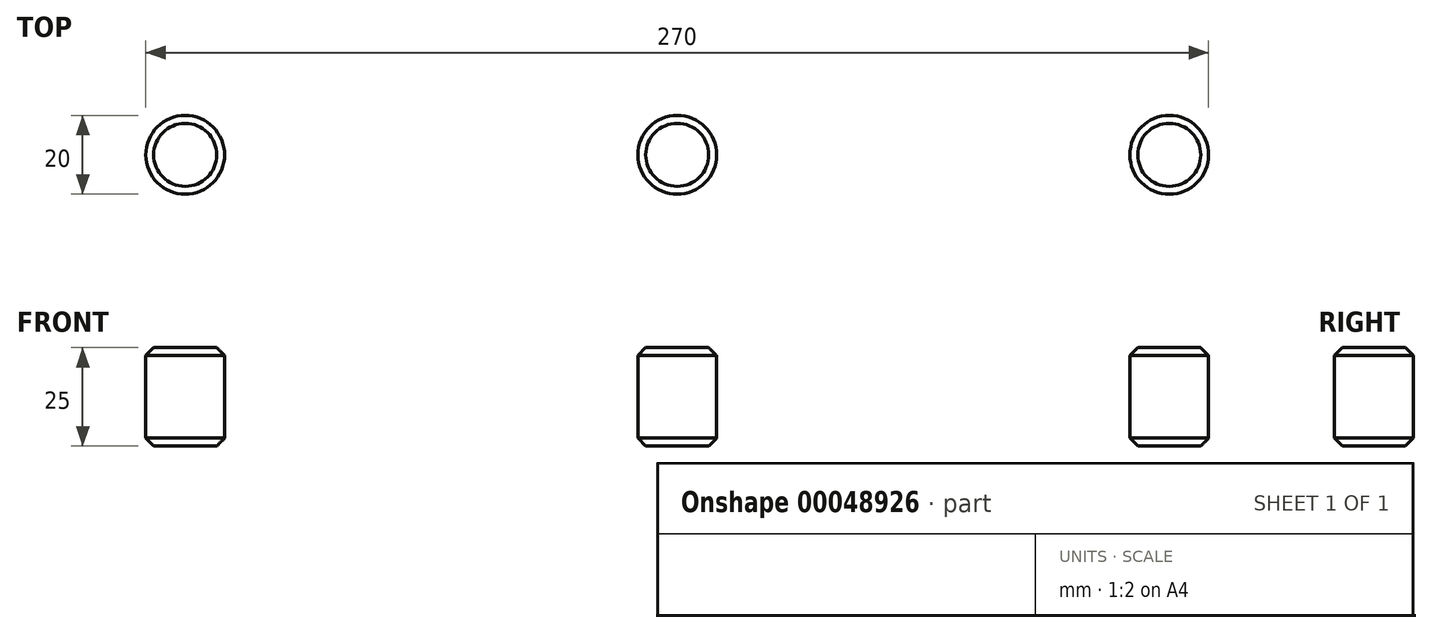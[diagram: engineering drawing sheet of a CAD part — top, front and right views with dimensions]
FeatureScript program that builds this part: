
annotation { "Feature Type Name" : "Feature", "Feature Type Description" : "" }
export const myFeature = defineFeature(function(context is Context, id is Id, definition is map)
    precondition{}
    {
        {
            var Q0;
            Q0=qCreatedBy(makeId("Top.planeOp"),FACE);
            var sketch = newSketch(context, id + "F0", { "sketchPlane" : qUnion([Q0])});
            skLineSegment(sketch, "E0.rect.bottom", {"start": v(-150, 90) * mm, "end": v(150, 90) * mm});
            skLineSegment(sketch, "E0.rect.top", {"start": v(-150, -90) * mm, "end": v(150, -90) * mm});
            skLineSegment(sketch, "E0.rect.left", {"start": v(-150, 90) * mm, "end": v(-150, -90) * mm});
            skLineSegment(sketch, "E0.rect.right", {"start": v(150, 90) * mm, "end": v(150, -90) * mm});
            skPoint(sketch, "E0.rect.middle", {"position": v(0, 0) * mm});
            skSolve(sketch);
        }
        {
            var Q0;
            Q0=makeQuery(id+"F0.imprint","IMPRINT",FACE,{"disambiguationData":[TD([[makeQuery(id+"F0.imprint","IMPRINT",EDGE,{"derivedFrom":sQuery(id+"F0.wireOp",EDGE,"E0.rect.bottom")}),-1.0]])]});
            extrude(context, id + "F1", {"entities" : qUnion([Q0]), "depth" : 25 * mm});
        }
        {
            var Q0;
            Q0=makeQuery(id+"F1.opExtrude","CAP_FACE",FACE,{"disambiguationData":[OSD([sQuery(id+"F0.wireOp",EDGE,"E0.rect.bottom"),sQuery(id+"F0.wireOp",EDGE,"E0.rect.top"),sQuery(id+"F0.wireOp",EDGE,"E0.rect.left"),sQuery(id+"F0.wireOp",EDGE,"E0.rect.right")])],"isStart":false});
            var sketch = newSketch(context, id + "F2", { "sketchPlane" : qUnion([Q0])});
            skLineSegment(sketch, "E1.rect.bottom", {"start": v(-125, 65) * mm, "end": v(125, 65) * mm, "construction": true});
            skLineSegment(sketch, "E1.rect.top", {"start": v(-125, -65) * mm, "end": v(125, -65) * mm, "construction": true});
            skLineSegment(sketch, "E1.rect.left", {"start": v(-125, 65) * mm, "end": v(-125, -65) * mm, "construction": true});
            skLineSegment(sketch, "E1.rect.right", {"start": v(125, 65) * mm, "end": v(125, -65) * mm, "construction": true});
            skPoint(sketch, "E1.rect.middle", {"position": v(0, 0) * mm});
            skCircle(sketch, "E2", {"center": v(-125, 65) * mm, "radius": 10 * mm});
            skCircle(sketch, "E3", {"center": v(0, 65) * mm, "radius": 10 * mm});
            skCircle(sketch, "E4", {"center": v(125, 65) * mm, "radius": 10 * mm});
            skLineSegment(sketch, "E5", {"start": v(0, 0) * mm, "end": v(-125, 0) * mm, "construction": true});
            skCircle(sketch, "E6.MirrorC", {"center": v(125, -65) * mm, "radius": 10 * mm});
            skCircle(sketch, "E7.MirrorC", {"center": v(0, -65) * mm, "radius": 10 * mm});
            skCircle(sketch, "E8.MirrorC", {"center": v(-125, -65) * mm, "radius": 10 * mm});
            skSolve(sketch);
        }
        {
            var Q0;
            Q0=makeQuery(id+"F2.imprint","IMPRINT",FACE,{"disambiguationData":[TD([[makeQuery(id+"F2.imprint","IMPRINT",EDGE,{"derivedFrom":sQuery(id+"F2.wireOp",EDGE,"E2")}),1.0]])]});
            var Q1;
            Q1=makeQuery(id+"F2.imprint","IMPRINT",FACE,{"disambiguationData":[TD([[makeQuery(id+"F2.imprint","IMPRINT",EDGE,{"derivedFrom":sQuery(id+"F2.wireOp",EDGE,"E3")}),1.0]])]});
            var Q2;
            Q2=makeQuery(id+"F2.imprint","IMPRINT",FACE,{"disambiguationData":[TD([[makeQuery(id+"F2.imprint","IMPRINT",EDGE,{"derivedFrom":sQuery(id+"F2.wireOp",EDGE,"E4")}),1.0]])]});
            var Q3;
            Q3=makeQuery(id+"F2.imprint","IMPRINT",FACE,{"disambiguationData":[TD([[makeQuery(id+"F2.imprint","IMPRINT",EDGE,{"derivedFrom":sQuery(id+"F2.wireOp",EDGE,"E6.MirrorC")}),-1.0]])]});
            var Q4;
            Q4=makeQuery(id+"F2.imprint","IMPRINT",FACE,{"disambiguationData":[TD([[makeQuery(id+"F2.imprint","IMPRINT",EDGE,{"derivedFrom":sQuery(id+"F2.wireOp",EDGE,"E7.MirrorC")}),-1.0]])]});
            var Q5;
            Q5=makeQuery(id+"F2.imprint","IMPRINT",FACE,{"disambiguationData":[TD([[makeQuery(id+"F2.imprint","IMPRINT",EDGE,{"derivedFrom":sQuery(id+"F2.wireOp",EDGE,"E8.MirrorC")}),-1.0]])]});
            var Q6;
            Q6=sQuery(id+"F2.wireOp",EDGE,"E2");
            var Q7;
            Q7=sQuery(id+"F2.wireOp",EDGE,"E3");
            var Q8;
            Q8=sQuery(id+"F2.wireOp",EDGE,"E4");
            var Q9;
            Q9=sQuery(id+"F2.wireOp",EDGE,"E6.MirrorC");
            var Q10;
            Q10=sQuery(id+"F2.wireOp",EDGE,"E7.MirrorC");
            var Q11;
            Q11=sQuery(id+"F2.wireOp",EDGE,"E8.MirrorC");
            extrude(context, id + "F3", {"entities" : qUnion([Q0, Q1, Q2, Q3, Q4, Q5]), "operationType" : NewBodyOperationType.REMOVE, "surfaceEntities" : qUnion([Q6, Q7, Q8, Q9, Q10, Q11]), "endBound" : BoundingType.THROUGH_ALL, "oppositeDirection" : true, "depth" : 25 * mm});
        }
        {
            var Q0;
            Q0=makeQuery(id+"F1.opExtrude","CAP_FACE",FACE,{"disambiguationData":[OSD([sQuery(id+"F0.wireOp",EDGE,"E0.rect.bottom"),sQuery(id+"F0.wireOp",EDGE,"E0.rect.top"),sQuery(id+"F0.wireOp",EDGE,"E0.rect.left"),sQuery(id+"F0.wireOp",EDGE,"E0.rect.right")])],"isStart":false});
            var Q1;
            Q1=makeQuery(id+"F1.opExtrude","CAP_FACE",FACE,{"disambiguationData":[OSD([sQuery(id+"F0.wireOp",EDGE,"E0.rect.bottom"),sQuery(id+"F0.wireOp",EDGE,"E0.rect.top"),sQuery(id+"F0.wireOp",EDGE,"E0.rect.left"),sQuery(id+"F0.wireOp",EDGE,"E0.rect.right")])],"isStart":true});
            chamfer(context, id + "F4", {"entities" : qUnion([Q0, Q1]), "chamferType" : ChamferType.OFFSET_ANGLE, "width" : 2 * mm, "oppositeDirection" : false, "angle" : 45 * degree, "tangentPropagation" : true});
        }
    });
